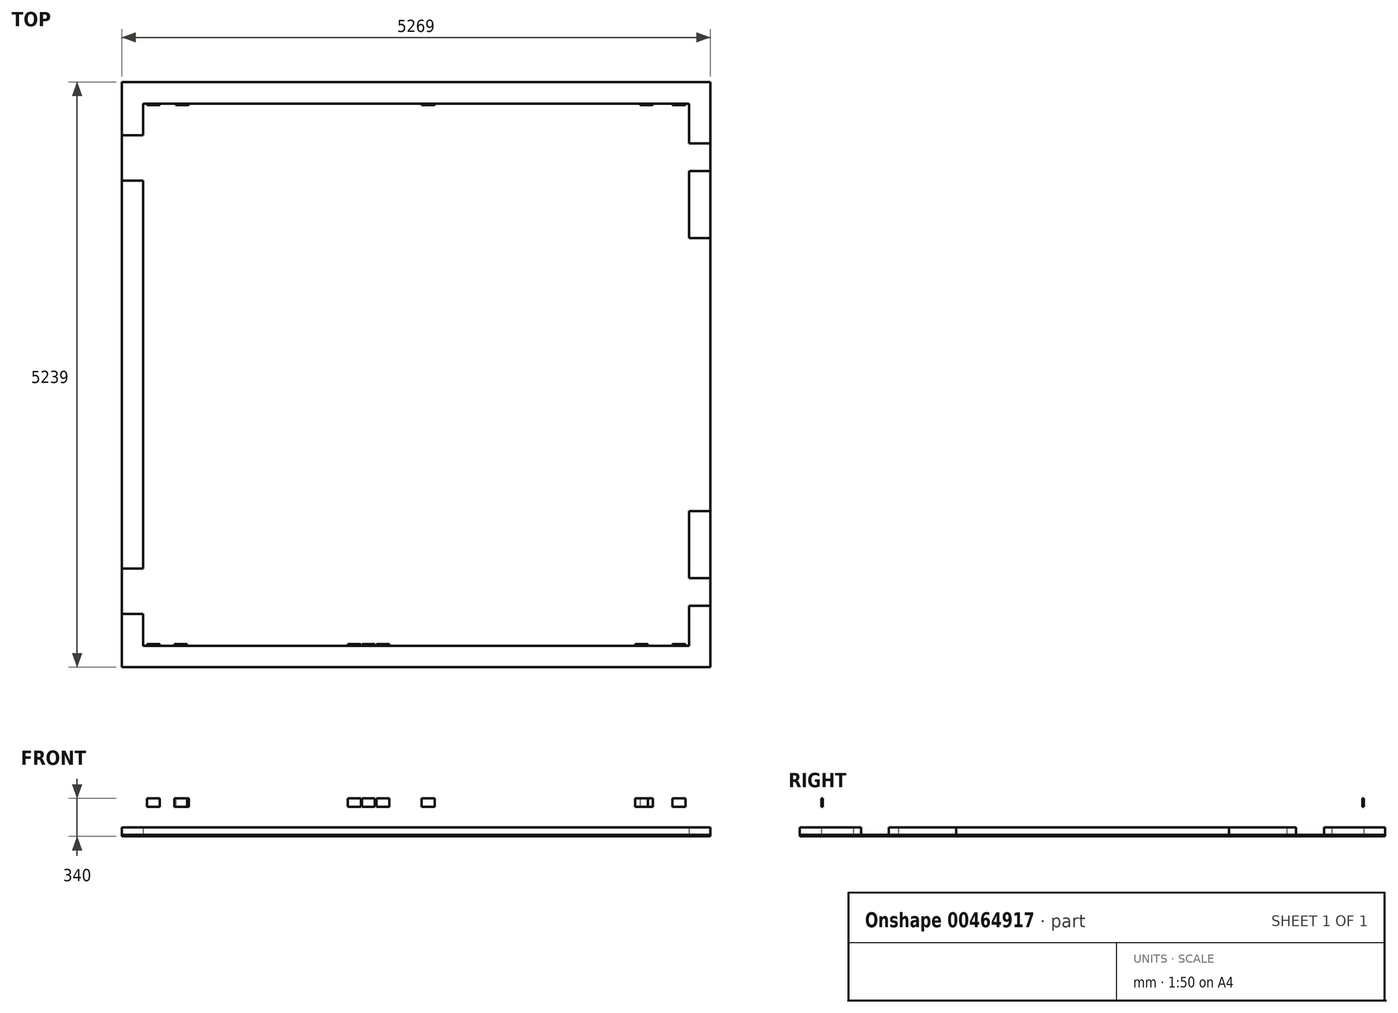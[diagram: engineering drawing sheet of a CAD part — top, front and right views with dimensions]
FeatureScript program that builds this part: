
annotation { "Feature Type Name" : "Feature", "Feature Type Description" : "" }
export const myFeature = defineFeature(function(context is Context, id is Id, definition is map)
    precondition{}
    {
        {
            var Q0;
            Q0=qCreatedBy(makeId("Top.planeOp"),FACE);
            cPlane(context, id + "F0", {"entities" : qUnion([Q0]), "cplaneType" : CPlaneType.OFFSET, "offset" : 250 * mm, "width" : 150 * mm, "height" : 150 * mm});
        }
        {
            var Q0;
            Q0=qCreatedBy(makeId("Top.planeOp"),FACE);
            var sketch = newSketch(context, id + "F1", { "sketchPlane" : qUnion([Q0])});
            skLineSegment(sketch, "E0.bottom", {"start": v(-2442.5, 0) * mm, "end": v(2442.5, 0) * mm});
            skLineSegment(sketch, "E0.top", {"start": v(-2442.5, 4855) * mm, "end": v(2442.5, 4855) * mm});
            skLineSegment(sketch, "E0.left", {"start": v(-2442.5, 0) * mm, "end": v(-2442.5, 285) * mm});
            skLineSegment(sketch, "E0.right", {"start": v(2442.5, 0) * mm, "end": v(2442.5, 357) * mm});
            skLineSegment(sketch, "E1", {"start": v(0, 0) * mm, "end": v(0, 4855) * mm, "construction": true});
            skLineSegment(sketch, "E2.0", {"start": v(-2634.5, -192) * mm, "end": v(-2634.5, 285) * mm});
            skLineSegment(sketch, "E2.1", {"start": v(-2634.5, -192) * mm, "end": v(2634.5, -192) * mm});
            skLineSegment(sketch, "E2.2", {"start": v(2634.5, -192) * mm, "end": v(2634.5, 357) * mm});
            skLineSegment(sketch, "E2.3", {"start": v(-2634.5, 5047) * mm, "end": v(2634.5, 5047) * mm});
            skLineSegment(sketch, "E3", {"start": v(-2442.5, 2427.5) * mm, "end": v(2442.5, 2427.5) * mm, "construction": true});
            skLineSegment(sketch, "E4", {"start": v(2442.5, 1206) * mm, "end": v(2634.5, 1206) * mm});
            skLineSegment(sketch, "E5", {"start": v(2442.5, 605) * mm, "end": v(2634.5, 605) * mm});
            skLineSegment(sketch, "E6", {"start": v(2442.5, 357) * mm, "end": v(2634.5, 357) * mm});
            skLineSegment(sketch, "E7.MirrorCS", {"start": v(2442.5, 4498) * mm, "end": v(2634.5, 4498) * mm});
            skLineSegment(sketch, "E8.MirrorCS", {"start": v(2442.5, 3649) * mm, "end": v(2634.5, 3649) * mm});
            skLineSegment(sketch, "E9.MirrorCS", {"start": v(2442.5, 4250) * mm, "end": v(2634.5, 4250) * mm});
            skLineSegment(sketch, "E10.trimOffspring", {"start": v(2442.5, 605) * mm, "end": v(2442.5, 1206) * mm});
            skLineSegment(sketch, "E11.trimOffspring", {"start": v(2634.5, 605) * mm, "end": v(2634.5, 1206) * mm});
            skLineSegment(sketch, "E12.trimOffspring", {"start": v(2442.5, 3649) * mm, "end": v(2442.5, 4250) * mm});
            skLineSegment(sketch, "E13.trimOffspring", {"start": v(2634.5, 3649) * mm, "end": v(2634.5, 4250) * mm});
            skLineSegment(sketch, "E14.trimOffspring", {"start": v(2634.5, 4498) * mm, "end": v(2634.5, 5047) * mm});
            skLineSegment(sketch, "E15.trimOffspring", {"start": v(2442.5, 4498) * mm, "end": v(2442.5, 4855) * mm});
            skLineSegment(sketch, "E16", {"start": v(-2634.5, 285) * mm, "end": v(-2442.5, 285) * mm});
            skLineSegment(sketch, "E17", {"start": v(-2442.5, 690) * mm, "end": v(-2634.5, 690) * mm});
            skLineSegment(sketch, "E18.MirrorCS", {"start": v(-2634.5, 4570) * mm, "end": v(-2442.5, 4570) * mm});
            skLineSegment(sketch, "E19.MirrorCS", {"start": v(-2442.5, 4165) * mm, "end": v(-2634.5, 4165) * mm});
            skLineSegment(sketch, "E20.trimOffspring", {"start": v(-2442.5, 690) * mm, "end": v(-2442.5, 4165) * mm});
            skLineSegment(sketch, "E21.trimOffspring", {"start": v(-2634.5, 690) * mm, "end": v(-2634.5, 4165) * mm});
            skLineSegment(sketch, "E22.trimOffspring", {"start": v(-2634.5, 4570) * mm, "end": v(-2634.5, 5047) * mm});
            skLineSegment(sketch, "E23.trimOffspring", {"start": v(-2442.5, 4570) * mm, "end": v(-2442.5, 4855) * mm});
            skLineSegment(sketch, "E24", {"start": v(-2488.5, 285) * mm, "end": v(-2488.5, 690) * mm});
            skLineSegment(sketch, "E25", {"start": v(-2588.5, 690) * mm, "end": v(-2588.5, 285) * mm});
            skPoint(sketch, "E25.endSnap0", {"position": v(-2538.5, 285) * mm});
            skLineSegment(sketch, "E26", {"start": v(-2538.5, 285) * mm, "end": v(-2538.5, 690) * mm, "construction": true});
            skLineSegment(sketch, "E27.MirrorCS", {"start": v(-2588.5, 285) * mm, "end": v(-2588.5, 690) * mm});
            skLineSegment(sketch, "E28.MirrorCS", {"start": v(-2488.5, 690) * mm, "end": v(-2488.5, 285) * mm});
            skLineSegment(sketch, "E29.MirrorCS", {"start": v(-2488.5, 4165) * mm, "end": v(-2488.5, 4570) * mm});
            skLineSegment(sketch, "E30.MirrorCS", {"start": v(-2588.5, 4165) * mm, "end": v(-2588.5, 4570) * mm});
            skLineSegment(sketch, "E31", {"start": v(-2538.5, 4165) * mm, "end": v(-2538.5, 4570) * mm, "construction": true});
            skSolve(sketch);
        }
        {
            var Q0;
            Q0=qCreatedBy(id+"F0.planeOp",FACE);
            var sketch = newSketch(context, id + "F2", { "sketchPlane" : qUnion([Q0])});
            skCircle(sketch, "E32", {"center": v(2352.5, 0) * mm, "radius": 57.5 * mm, "construction": true});
            skCircle(sketch, "E33", {"center": v(-2352.5, 0) * mm, "radius": 57.5 * mm, "construction": true});
            skCircle(sketch, "E34.MirrorC", {"center": v(2352.5, 4855) * mm, "radius": 57.5 * mm, "construction": true});
            skCircle(sketch, "E35.MirrorC", {"center": v(-2352.5, 4855) * mm, "radius": 57.5 * mm, "construction": true});
            skLineSegment(sketch, "E36.bottom", {"start": v(2295, 0) * mm, "end": v(2410, 0) * mm});
            skLineSegment(sketch, "E36.top", {"start": v(2295, 14) * mm, "end": v(2410, 14) * mm});
            skLineSegment(sketch, "E36.left", {"start": v(2295, 0) * mm, "end": v(2295, 14) * mm});
            skLineSegment(sketch, "E36.right", {"start": v(2410, 0) * mm, "end": v(2410, 14) * mm});
            skLineSegment(sketch, "E37", {"start": v(2352.5, 0) * mm, "end": v(2352.5, 14) * mm, "construction": true});
            skLineSegment(sketch, "E38.bottom", {"start": v(-2295, 0) * mm, "end": v(-2410, 0) * mm});
            skLineSegment(sketch, "E38.top", {"start": v(-2295, 14) * mm, "end": v(-2410, 14) * mm});
            skLineSegment(sketch, "E38.left", {"start": v(-2295, 0) * mm, "end": v(-2295, 14) * mm});
            skLineSegment(sketch, "E38.right", {"start": v(-2410, 0) * mm, "end": v(-2410, 14) * mm});
            skLineSegment(sketch, "E39", {"start": v(-2352.5, 0) * mm, "end": v(-2352.5, 14) * mm, "construction": true});
            skLineSegment(sketch, "E40.bottom", {"start": v(-2410, 4855) * mm, "end": v(-2295, 4855) * mm});
            skLineSegment(sketch, "E40.top", {"start": v(-2410, 4841) * mm, "end": v(-2295, 4841) * mm});
            skLineSegment(sketch, "E40.left", {"start": v(-2410, 4855) * mm, "end": v(-2410, 4841) * mm});
            skLineSegment(sketch, "E40.right", {"start": v(-2295, 4855) * mm, "end": v(-2295, 4841) * mm});
            skLineSegment(sketch, "E41", {"start": v(-2352.5, 4855) * mm, "end": v(-2352.5, 4841) * mm, "construction": true});
            skLineSegment(sketch, "E42.bottom", {"start": v(2295, 4855) * mm, "end": v(2410, 4855) * mm});
            skLineSegment(sketch, "E42.top", {"start": v(2295, 4841) * mm, "end": v(2410, 4841) * mm});
            skLineSegment(sketch, "E42.left", {"start": v(2295, 4855) * mm, "end": v(2295, 4841) * mm});
            skLineSegment(sketch, "E42.right", {"start": v(2410, 4855) * mm, "end": v(2410, 4841) * mm});
            skLineSegment(sketch, "E43", {"start": v(2352.5, 4855) * mm, "end": v(2352.5, 4841) * mm, "construction": true});
            skSolve(sketch);
        }
        {
            var Q0;
            Q0=qCreatedBy(id+"F0.planeOp",FACE);
            var sketch = newSketch(context, id + "F3", { "sketchPlane" : qUnion([Q0])});
            skCircle(sketch, "E44", {"center": v(2017.5, 0) * mm, "radius": 57.5 * mm, "construction": true});
            skCircle(sketch, "E45.MirrorC", {"center": v(-2107.5, 0) * mm, "radius": 57.5 * mm, "construction": true});
            skCircle(sketch, "E46", {"center": v(2062.5, 4855) * mm, "radius": 57.5 * mm, "construction": true});
            skCircle(sketch, "E47", {"center": v(-2092.5, 4855) * mm, "radius": 57.5 * mm, "construction": true});
            skCircle(sketch, "E48", {"center": v(107.5, 4855) * mm, "radius": 57.5 * mm, "construction": true});
            skCircle(sketch, "E49", {"center": v(-427.5, 0) * mm, "radius": 57.5 * mm, "construction": true});
            skCircle(sketch, "E50", {"center": v(-552.5, 0) * mm, "radius": 57.5 * mm, "construction": true});
            skLineSegment(sketch, "E51.bottom", {"start": v(1960, 0) * mm, "end": v(2075, 0) * mm});
            skLineSegment(sketch, "E51.top", {"start": v(1960, 14) * mm, "end": v(2075, 14) * mm});
            skLineSegment(sketch, "E51.left", {"start": v(1960, 0) * mm, "end": v(1960, 14) * mm});
            skLineSegment(sketch, "E51.right", {"start": v(2075, 0) * mm, "end": v(2075, 14) * mm});
            skLineSegment(sketch, "E52", {"start": v(2017.5, 0) * mm, "end": v(2017.5, 14) * mm, "construction": true});
            skLineSegment(sketch, "E53.bottom", {"start": v(-485, 0) * mm, "end": v(-370, 0) * mm});
            skLineSegment(sketch, "E53.top", {"start": v(-485, 14) * mm, "end": v(-370, 14) * mm});
            skLineSegment(sketch, "E53.left", {"start": v(-485, 0) * mm, "end": v(-485, 14) * mm});
            skLineSegment(sketch, "E53.right", {"start": v(-370, 0) * mm, "end": v(-370, 14) * mm});
            skLineSegment(sketch, "E54.bottom", {"start": v(-610, 0) * mm, "end": v(-495, 0) * mm});
            skLineSegment(sketch, "E54.top", {"start": v(-610, 14) * mm, "end": v(-495, 14) * mm});
            skLineSegment(sketch, "E54.left", {"start": v(-610, 0) * mm, "end": v(-610, 14) * mm});
            skLineSegment(sketch, "E54.right", {"start": v(-495, 0) * mm, "end": v(-495, 14) * mm});
            skLineSegment(sketch, "E55", {"start": v(-552.5, 0) * mm, "end": v(-552.5, 14) * mm, "construction": true});
            skLineSegment(sketch, "E56", {"start": v(-427.5, 0) * mm, "end": v(-427.5, 14) * mm, "construction": true});
            skLineSegment(sketch, "E57.bottom", {"start": v(-2165, 0) * mm, "end": v(-2050, 0) * mm});
            skLineSegment(sketch, "E57.top", {"start": v(-2165, 14) * mm, "end": v(-2050, 14) * mm});
            skLineSegment(sketch, "E57.left", {"start": v(-2165, 0) * mm, "end": v(-2165, 14) * mm});
            skLineSegment(sketch, "E57.right", {"start": v(-2050, 0) * mm, "end": v(-2050, 14) * mm});
            skLineSegment(sketch, "E58", {"start": v(-2107.5, 0) * mm, "end": v(-2107.5, 14) * mm, "construction": true});
            skLineSegment(sketch, "E59.bottom", {"start": v(-2150, 4841) * mm, "end": v(-2035, 4841) * mm});
            skLineSegment(sketch, "E59.top", {"start": v(-2150, 4855) * mm, "end": v(-2035, 4855) * mm});
            skLineSegment(sketch, "E59.left", {"start": v(-2150, 4841) * mm, "end": v(-2150, 4855) * mm});
            skLineSegment(sketch, "E59.right", {"start": v(-2035, 4841) * mm, "end": v(-2035, 4855) * mm});
            skLineSegment(sketch, "E60", {"start": v(-2092.5, 4841) * mm, "end": v(-2092.5, 4855) * mm, "construction": true});
            skLineSegment(sketch, "E61.bottom", {"start": v(50, 4841) * mm, "end": v(165, 4841) * mm});
            skLineSegment(sketch, "E61.top", {"start": v(50, 4855) * mm, "end": v(165, 4855) * mm});
            skLineSegment(sketch, "E61.left", {"start": v(50, 4841) * mm, "end": v(50, 4855) * mm});
            skLineSegment(sketch, "E61.right", {"start": v(165, 4841) * mm, "end": v(165, 4855) * mm});
            skLineSegment(sketch, "E62", {"start": v(107.5, 4841) * mm, "end": v(107.5, 4855) * mm, "construction": true});
            skLineSegment(sketch, "E63.bottom", {"start": v(2005, 4841) * mm, "end": v(2120, 4841) * mm});
            skLineSegment(sketch, "E63.top", {"start": v(2005, 4855) * mm, "end": v(2120, 4855) * mm});
            skLineSegment(sketch, "E63.left", {"start": v(2005, 4841) * mm, "end": v(2005, 4855) * mm});
            skLineSegment(sketch, "E63.right", {"start": v(2120, 4841) * mm, "end": v(2120, 4855) * mm});
            skLineSegment(sketch, "E64", {"start": v(2062.5, 4841) * mm, "end": v(2062.5, 4855) * mm, "construction": true});
            skSolve(sketch);
        }
        {
            var Q0;
            Q0=qCreatedBy(id+"F0.planeOp",FACE);
            var sketch = newSketch(context, id + "F4", { "sketchPlane" : qUnion([Q0])});
            skCircle(sketch, "E65", {"center": v(-297.5, 0) * mm, "radius": 57.5 * mm, "construction": true});
            skLineSegment(sketch, "E66.bottom", {"start": v(-355, 0) * mm, "end": v(-240, 0) * mm});
            skLineSegment(sketch, "E66.top", {"start": v(-355, 14) * mm, "end": v(-240, 14) * mm});
            skLineSegment(sketch, "E66.left", {"start": v(-355, 0) * mm, "end": v(-355, 14) * mm});
            skLineSegment(sketch, "E66.right", {"start": v(-240, 0) * mm, "end": v(-240, 14) * mm});
            skLineSegment(sketch, "E67", {"start": v(-297.5, 0) * mm, "end": v(-297.5, 14) * mm, "construction": true});
            skSolve(sketch);
        }
        {
            var Q0;
            Q0=makeQuery(id+"F1.imprint","IMPRINT",FACE,{"disambiguationData":[TD([[makeQuery(id+"F1.imprint","IMPRINT",EDGE,{"derivedFrom":sQuery(id+"F1.wireOp",EDGE,"E4")}),-1.0]])]});
            var Q1;
            Q1=makeQuery(id+"F1.imprint","IMPRINT",FACE,{"disambiguationData":[TD([[makeQuery(id+"F1.imprint","IMPRINT",EDGE,{"derivedFrom":sQuery(id+"F1.wireOp",EDGE,"E8.MirrorCS")}),1.0]])]});
            var Q2;
            Q2=makeQuery(id+"F1.imprint","IMPRINT",FACE,{"disambiguationData":[TD([[makeQuery(id+"F1.imprint","IMPRINT",EDGE,{"derivedFrom":sQuery(id+"F1.wireOp",EDGE,"E0.top")}),1.0]])]});
            var Q3;
            {var subQ3=sQuery(id+"F1.wireOp",EDGE,"E20.trimOffspring");Q3=makeQuery(id+"F1.imprint","IMPRINT",FACE,{"disambiguationData":[TD([[makeQuery(id+"F1.imprint","IMPRINT",EDGE,{"derivedFrom":subQ3}),1.0]])]});}
            var Q4;
            Q4=makeQuery(id+"F1.imprint","IMPRINT",FACE,{"disambiguationData":[TD([[makeQuery(id+"F1.imprint","IMPRINT",EDGE,{"derivedFrom":sQuery(id+"F1.wireOp",EDGE,"E0.bottom")}),-1.0]])]});
            extrude(context, id + "F5", {"entities" : qUnion([Q0, Q1, Q2, Q3, Q4]), "depth" : 66 * mm});
        }
        {
            var Q0;
            Q0=qCreatedBy(makeId("Top.planeOp"),FACE);
            var sketch = newSketch(context, id + "F6", { "sketchPlane" : qUnion([Q0])});
            skLineSegment(sketch, "E68.bottom", {"start": v(-2634.5, -192) * mm, "end": v(2634.5, -192) * mm});
            skLineSegment(sketch, "E68.top", {"start": v(-2634.5, 5047) * mm, "end": v(2634.5, 5047) * mm});
            skLineSegment(sketch, "E68.left", {"start": v(-2634.5, -192) * mm, "end": v(-2634.5, 5047) * mm});
            skLineSegment(sketch, "E68.right", {"start": v(2634.5, -192) * mm, "end": v(2634.5, 5047) * mm});
            skSolve(sketch);
        }
        {
            var Q0;
            Q0 = qSketchRegion(id + "F6", true);
            extrude(context, id + "F7", {"entities" : qUnion([Q0]), "oppositeDirection" : true, "depth" : 15 * mm});
        }
        {
            var Q0;
            Q0 = qSketchRegion(id + "F2", true);
            extrude(context, id + "F8", {"entities" : qUnion([Q0]), "depth" : 75 * mm});
        }
        {
            var Q0;
            Q0 = qSketchRegion(id + "F3", true);
            extrude(context, id + "F9", {"entities" : qUnion([Q0]), "depth" : 75 * mm});
        }
        {
            var Q0;
            Q0 = qSketchRegion(id + "F4", true);
            extrude(context, id + "F10", {"entities" : qUnion([Q0]), "depth" : 75 * mm});
        }
    });
